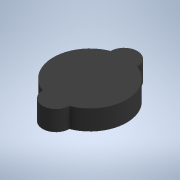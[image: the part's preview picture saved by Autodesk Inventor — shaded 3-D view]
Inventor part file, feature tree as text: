
AUTODESK INVENTOR PART (.ipt)
format: ipt  version: 2020 (Build 240168000, 168)  size: 104,960 bytes
history: native  units: mm
features: extrude x1, sketch x1
ambient origin geometry x8: Origin, YZ Plane, XZ Plane, XY Plane, X Axis, Y Axis, Z Axis, Center Point
bodies: Solid1 (feature_tree)
feature tree (2):
  extrude  "Extrusion1"  Depth=4.0mm
  sketch  "Sketch1"  dims[d0=22.0mm d1=4.0mm d2=6.0mm d3=0.0mm]
